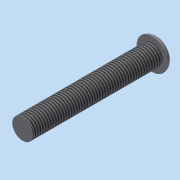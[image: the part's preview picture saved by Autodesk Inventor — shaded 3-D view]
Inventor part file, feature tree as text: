
AUTODESK INVENTOR PART (.ipt)
format: ipt  version: 2015 (Build 190159000, 159)  size: 95,744 bytes
history: native  units: mm
features: revolve x1, fillet x1, thread x1, sketch x1
ambient origin geometry x8: Origin, YZ Plane, XZ Plane, XY Plane, X Axis, Y Axis, Z Axis, Center Point
bodies: Solid1 (feature_tree)
feature tree (4):
  revolve  "Revolution1"  [1 undecoded]
  fillet  "Fillet1"  Radius=1.0mm
  thread  "Thread1"  [1 undecoded]
  sketch  "Sketch1"  dims[d0=2.0mm d1=3.0mm d2=1.0mm d3=90.0deg d4=1.0mm d5=10.0mm d6=0.0mm d7=25.0mm]
note: 2 required parameter values undecoded (feature->parameter linkage not recoverable at this tier; creation-order binding heuristic only, values carry confidence <= 0.55)